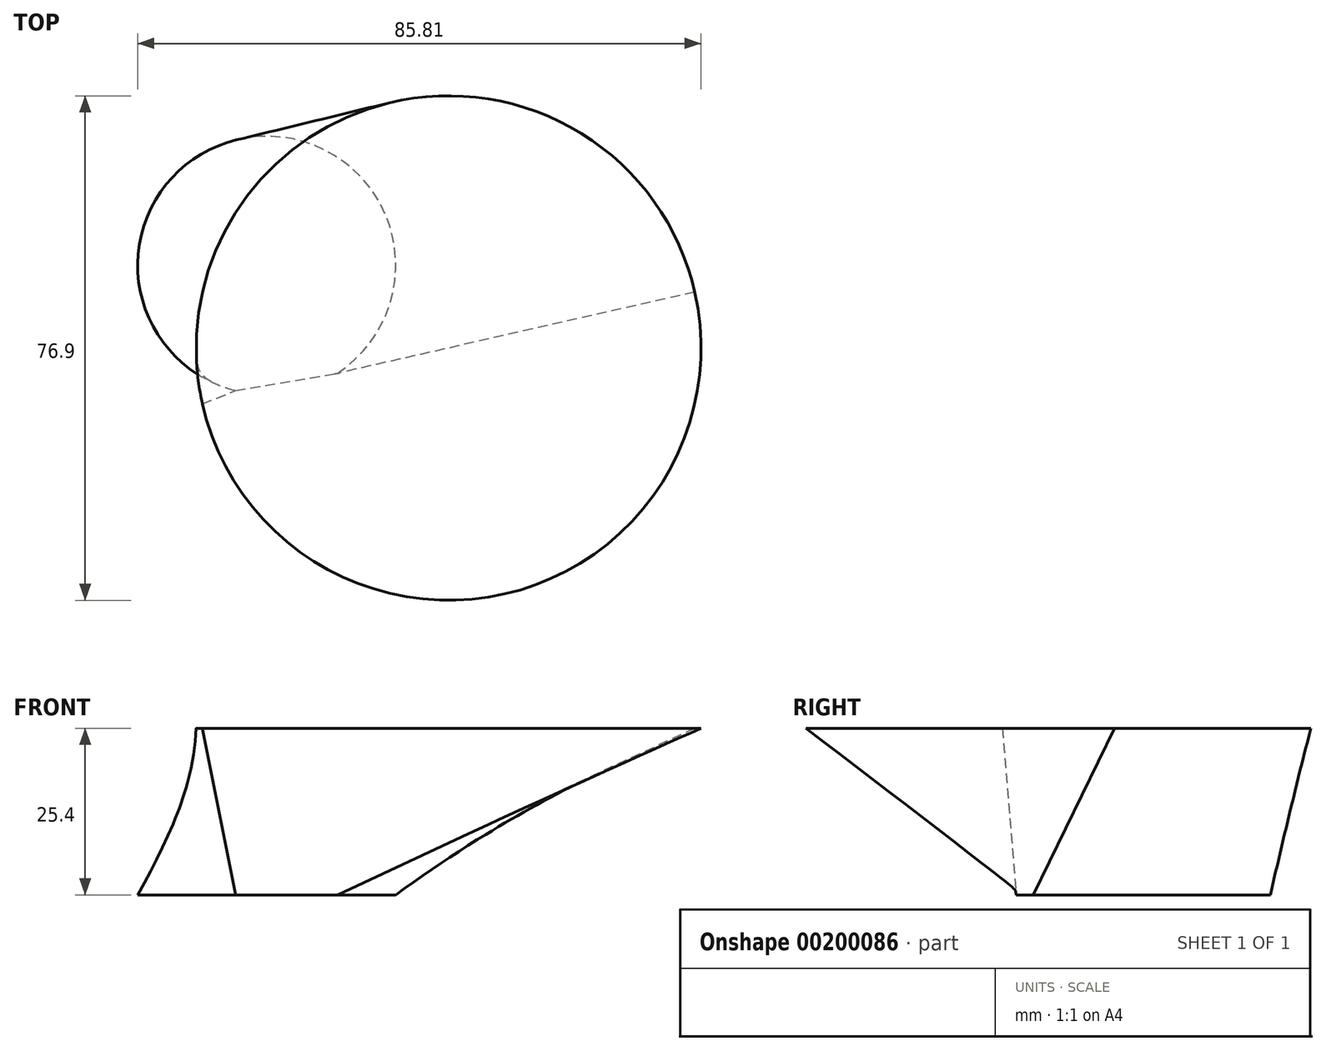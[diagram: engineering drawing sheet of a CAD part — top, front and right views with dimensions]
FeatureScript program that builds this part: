
annotation { "Feature Type Name" : "Feature", "Feature Type Description" : "" }
export const myFeature = defineFeature(function(context is Context, id is Id, definition is map)
    precondition{}
    {
        {
            var Q0;
            Q0=qCreatedBy(makeId("Top.planeOp"),FACE);
            cPlane(context, id + "F0", {"entities" : qUnion([Q0]), "cplaneType" : CPlaneType.OFFSET, "offset" : 25.4 * mm, "width" : 152.4 * mm, "height" : 152.4 * mm});
        }
        {
            var Q0;
            Q0=qCreatedBy(id+"F0.planeOp",FACE);
            var sketch = newSketch(context, id + "F1", { "sketchPlane" : qUnion([Q0])});
            skCircle(sketch, "E0", {"center": v(-23.81, -12.61) * mm, "radius": 38.45 * mm});
            skSolve(sketch);
        }
        {
            var Q0;
            Q0=qCreatedBy(makeId("Top.planeOp"),FACE);
            var sketch = newSketch(context, id + "F2", { "sketchPlane" : qUnion([Q0])});
            skCircle(sketch, "E1", {"center": v(-51.5, 0) * mm, "radius": 19.66 * mm});
            skLineSegment(sketch, "E2", {"start": v(-56.26, -19.08) * mm, "end": v(56.76, 0) * mm});
            skLineSegment(sketch, "E3", {"start": v(56.76, 0) * mm, "end": v(-9.57, -70.94) * mm});
            skLineSegment(sketch, "E4", {"start": v(-9.57, -70.94) * mm, "end": v(-93.06, -32.07) * mm});
            skLineSegment(sketch, "E5", {"start": v(-93.06, -32.07) * mm, "end": v(-36.04, 164.55) * mm});
            skLineSegment(sketch, "E6", {"start": v(-36.04, 164.55) * mm, "end": v(56.76, 0) * mm});
            skLineSegment(sketch, "E7", {"start": v(-56.26, -19.08) * mm, "end": v(-9.57, -70.94) * mm});
            skSolve(sketch);
        }
        {
            var Q0;
            Q0=makeQuery(id+"F1.imprint","IMPRINT",FACE,{"disambiguationData":[TD([[makeQuery(id+"F1.imprint","IMPRINT",EDGE,{"derivedFrom":sQuery(id+"F1.wireOp",EDGE,"E0")}),1.0]])]});
            var Q1;
            {var subQ0=sQuery(id+"F2.wireOp",EDGE,"E2");var subQ1=sQuery(id+"F2.wireOp",EDGE,"E1");var subQ3=makeQuery(id+"F2.imprint","INTERSECT",VERTEX,{"derivedFrom":[subQ1,subQ0]});Q1=makeQuery(id+"F2.imprint","IMPRINT",FACE,{"disambiguationData":[TD([[makeQuery(id+"F2.imprint","IMPRINT",EDGE,{"disambiguationData":[TD([[subQ3,-1.0]])],"derivedFrom":subQ1}),1.0]])]});}
            loft(context, id + "F3", {"sheetProfilesArray" : [{ "sheetProfileEntities" : qUnion([Q0]) }, { "sheetProfileEntities" : qUnion([Q1]) }]});
        }
    });
